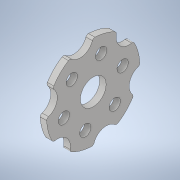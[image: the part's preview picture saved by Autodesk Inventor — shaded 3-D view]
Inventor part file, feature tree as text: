
AUTODESK INVENTOR PART (.ipt)
format: ipt  version: 2021 (Build 250183000, 183)  size: 175,616 bytes
history: native  units: in
note: dims shown in document units (in); Inventor stores cm internally (conversion verified against a paired STEP export)
features: extrude x1, fillet x1, sketch x1
ambient origin geometry x8: Origin, YZ Plane, XZ Plane, XY Plane, X Axis, Y Axis, Z Axis, Center Point
bodies: Solid1 (feature_tree)
feature tree (3):
  extrude  "Extrusion1"  Depth=0.125in
  fillet  "Fillet1"  Radius=0.55in
  sketch  "Sketch1"  dims[d0=4.517in d1=2.952in d2=0.55in d3=45.0deg d4=2.3622in d6=360.0deg d8=1.25in d12=1.25in d16=15.0deg d17=2.3622in d19=360.0deg d21=0.3125in d22=0.0in d23=0.125in d24=0.851in d25=2.3676in]
